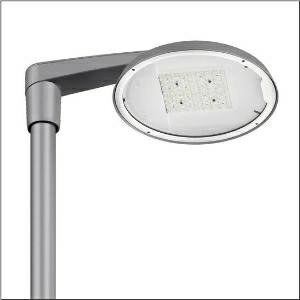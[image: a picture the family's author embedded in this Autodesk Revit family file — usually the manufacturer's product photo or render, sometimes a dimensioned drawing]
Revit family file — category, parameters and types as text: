
# Revit family: dl_r__50_iq_mini___st0_5a_5xa248b41f08me_b712
name_source: partatom
category: Lighting Fixtures
units: mm (PartAtom-declared; Revit-internal decimal feet)

## family parameters
Cut with Voids When Loaded = No
Host = Face
Light Source = No
Part Type = Normal
Room Calculation Point = No
Round Connector Dimension = Use Diameter
Shared = No

## types (1)
- --- (1 x LED, 15660 lm, 101.7 W, 4000K)
    Apparent Load = 102 VA
    CIE Flux Codes = 41 75 97 100 100
    Color Rendering = 70
    Color Temperature = 4000K
    Default Elevation = 1800 mm
    Description = DL® 50 iQ mini, mast luminaire, primary light control with lens, of PMMA, primary optical cover: cover, of toughened safety glass, transparent, light distribution: ST0.5a, light emission: direct distribution, primary light characteristic: asymmetric, installation type: side-entry, post-top, LED, High Power LED, rated luminous flux: 15.660lm, luminous efficacy: 154lm/W, light colour: 740, colour temperature: 4000K, control gear: iQ Street-Remote, control: optimised constant luminous flux control (CLO 2.0), Desk-Remote (wireless, voltage-free reading and setting of iQ features in the workshop via application-optimized NFC function/RFID function), Light-Fading, Smart-Wire, Night-Set, Lumen-Switch, Temp-Guard, Auto-Match, Street-Remote, mains connection: 230..240V, AC, 50/60Hz, connection cable pre-assembled, cable length: 10,5m, start of lifetime: 102W, end of service life: 111W, reduction: 45W, luminaire housing, of diecast aluminium, powder-coated, Siteco® metallic grey (DB 702S), inclination adjustable: 0°, 5°, 10° (post-top) | 0°, -5°, -10°, -15° (side-entry), please order mast post-top element or mast side-entry element separately, diameter: 500mm, height: 115mm, post-top: for spigot size d x l = 76 x 100mm; with reducer (optional accessory) 60 x 100mm | side-entry: for spigot size d x l = 60 x 100mm; with reducer (optional accessory) 42 x 100mm, mounting height: 4..6m, protection rating (complete): IP66, insulation class (complete): insulation class II (safety insulation), certification: CE, ENEC, ENEC+, VDE, impact resistance: IK08, permissible operating ambient temperature for outdoor applications: -25..+40°C, standard-compliant lighting for roads and squares, packaging unit: 1 piece

Light Distribution: ST0.5a
    Height = 115 mm
    Lamp = 1 x LED
    Lamp Light Flux = 15660 lm
    Lamp Power = 101.7 W
    Lamp count = 1
    Length = 500 mm
    Luminous efficacy = 154 lm/W
    Manufacturer = Siteco
    ModVariant = No
    Model = 5XA248B41F08ME
    Number of Poles = 1
    OnlyDefault = Yes
    Power Factor = 1
    Product Name = DL® 50 iQ mini | ST0.5a
    Product group = mast luminaire | pylon top
    ProductGroupID = 6100
    Protection Class = Protection class II
    Protection Degree = IP 66
    RLX_Detail_Level = 1
    RLX_Emergency_Light_Flux = 0 lm
    RLX_Emergency_Type = 0
    RLX_Emergency_Type_DB = No
    RlxData = <blob elided: 128281 chars, md5=88bd09f3>
    Socket = socket
    Standby Power = 0 W
    System Light Flux = 15660 lm
    System Power = 102 W
    Type Comments = factory setting: luminous flux: 100 % | dim-lin: 254 | 534 mA
    Type Image = l_1251790.jpg
    URL = http://relux.com
    VarID = @adj_164513
    Voltage = 0 V
    Weight = 0.00 kg
    Width = 0 mm  [stored 0 ft]

note: [stored X ft] marks values corroborated as IEEE doubles in the binary element streams (Revit-internal decimal feet)

## geometry (parser evidence)
native form markers: Blend x4, Sweep x11
no freeform markers — native parametric forms only
